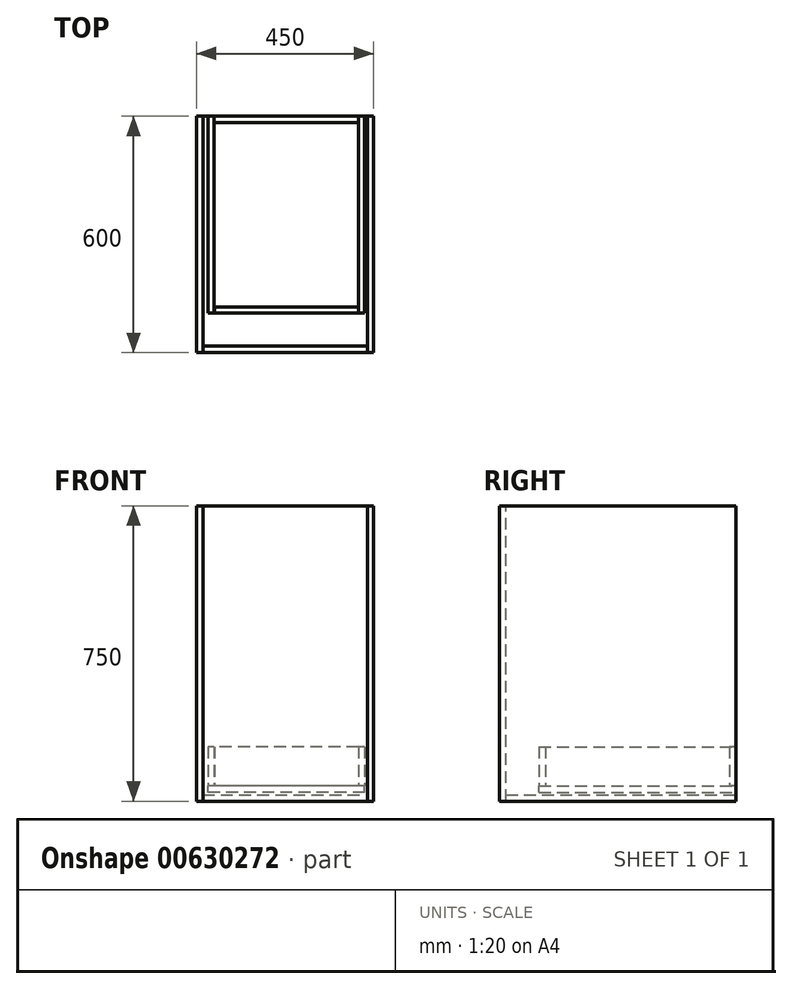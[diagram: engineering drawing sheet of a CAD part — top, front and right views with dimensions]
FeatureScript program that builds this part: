
annotation { "Feature Type Name" : "Feature", "Feature Type Description" : "" }
export const myFeature = defineFeature(function(context is Context, id is Id, definition is map)
    precondition{}
    {
        {
            var Q0;
            Q0=qCreatedBy(makeId("Top.planeOp"),FACE);
            var sketch = newSketch(context, id + "F0", { "sketchPlane" : qUnion([Q0])});
            skLineSegment(sketch, "E0.bottom", {"start": v(-209, -292) * mm, "end": v(209, -292) * mm});
            skLineSegment(sketch, "E0.top", {"start": v(-209, 292) * mm, "end": v(209, 292) * mm});
            skLineSegment(sketch, "E0.left", {"start": v(-209, -292) * mm, "end": v(-209, 292) * mm});
            skLineSegment(sketch, "E0.right", {"start": v(209, -292) * mm, "end": v(209, 292) * mm});
            skPoint(sketch, "E0.middle", {"position": v(0, 0) * mm});
            skSolve(sketch);
        }
        {
            var Q0;
            Q0 = qSketchRegion(id + "F0", true);
            extrude(context, id + "F1", {"entities" : qUnion([Q0]), "oppositeDirection" : true, "depth" : 16 * mm, "offsetDistance" : 25 * mm});
        }
        {
            var Q0;
            Q0=makeQuery(id+"F1.opExtrude","SWEPT_FACE",FACE,{"disambiguationData":[OSD([sQuery(id+"F0.wireOp",EDGE,"E0.bottom")])]});
            var sketch = newSketch(context, id + "F2", { "sketchPlane" : qUnion([Q0])});
            skLineSegment(sketch, "E1.bottom", {"start": v(-209, -16) * mm, "end": v(209, -16) * mm});
            skLineSegment(sketch, "E1.top", {"start": v(-209, 734) * mm, "end": v(209, 734) * mm});
            skLineSegment(sketch, "E1.left", {"start": v(-209, -16) * mm, "end": v(-209, 734) * mm});
            skLineSegment(sketch, "E1.right", {"start": v(209, -16) * mm, "end": v(209, 734) * mm});
            skSolve(sketch);
        }
        {
            var Q0;
            Q0 = qSketchRegion(id + "F2", true);
            extrude(context, id + "F3", {"entities" : qUnion([Q0]), "depth" : 16 * mm, "offsetDistance" : 25 * mm});
        }
        {
            var Q0;
            Q0=makeQuery(id+"F1.opExtrude","SWEPT_FACE",FACE,{"disambiguationData":[OSD([sQuery(id+"F0.wireOp",EDGE,"E0.right")])]});
            var sketch = newSketch(context, id + "F4", { "sketchPlane" : qUnion([Q0])});
            skLineSegment(sketch, "E2.bottom", {"start": v(292, -16) * mm, "end": v(-308, -16) * mm});
            skLineSegment(sketch, "E2.top", {"start": v(292, 734) * mm, "end": v(-308, 734) * mm});
            skLineSegment(sketch, "E2.left", {"start": v(292, -16) * mm, "end": v(292, 734) * mm});
            skLineSegment(sketch, "E2.right", {"start": v(-308, -16) * mm, "end": v(-308, 734) * mm});
            skSolve(sketch);
        }
        {
            var Q0;
            Q0 = qSketchRegion(id + "F4", true);
            extrude(context, id + "F5", {"entities" : qUnion([Q0]), "depth" : 16 * mm, "offsetDistance" : 25 * mm});
        }
        {
            var Q0;
            Q0=makeQuery(id+"F1.opExtrude","SWEPT_FACE",FACE,{"disambiguationData":[OSD([sQuery(id+"F0.wireOp",EDGE,"E0.left")])]});
            var sketch = newSketch(context, id + "F6", { "sketchPlane" : qUnion([Q0])});
            skLineSegment(sketch, "E3.bottom", {"start": v(-292, -16) * mm, "end": v(308, -16) * mm});
            skLineSegment(sketch, "E3.top", {"start": v(-292, 734) * mm, "end": v(308, 734) * mm});
            skLineSegment(sketch, "E3.left", {"start": v(-292, -16) * mm, "end": v(-292, 734) * mm});
            skLineSegment(sketch, "E3.right", {"start": v(308, -16) * mm, "end": v(308, 734) * mm});
            skSolve(sketch);
        }
        {
            var Q0;
            Q0 = qSketchRegion(id + "F6", true);
            extrude(context, id + "F7", {"entities" : qUnion([Q0]), "depth" : 16 * mm, "offsetDistance" : 25 * mm});
        }
        {
            var Q0;
            Q0=makeQuery(id+"F1.opExtrude","SWEPT_FACE",FACE,{"disambiguationData":[OSD([sQuery(id+"F0.wireOp",EDGE,"E0.top")])]});
            var sketch = newSketch(context, id + "F8", { "sketchPlane" : qUnion([Q0])});
            skLineSegment(sketch, "E4.bottom", {"start": v(-202.02, 6.24) * mm, "end": v(195.98, 6.24) * mm});
            skLineSegment(sketch, "E4.top", {"start": v(-202.02, 22.24) * mm, "end": v(195.98, 22.24) * mm});
            skLineSegment(sketch, "E4.left", {"start": v(-202.02, 6.24) * mm, "end": v(-202.02, 22.24) * mm});
            skLineSegment(sketch, "E4.right", {"start": v(195.98, 6.24) * mm, "end": v(195.98, 22.24) * mm});
            skSolve(sketch);
        }
        {
            var Q0;
            Q0 = qSketchRegion(id + "F8", true);
            extrude(context, id + "F9", {"entities" : qUnion([Q0]), "oppositeDirection" : true, "depth" : 500 * mm, "offsetDistance" : 25 * mm});
        }
        {
            var Q0;
            Q0=makeQuery(id+"F9.opExtrude","SWEPT_FACE",FACE,{"disambiguationData":[OSD([sQuery(id+"F8.wireOp",EDGE,"E4.top")])]});
            var sketch = newSketch(context, id + "F10", { "sketchPlane" : qUnion([Q0])});
            skLineSegment(sketch, "E5.bottom", {"start": v(202.02, -208) * mm, "end": v(186.02, -208) * mm});
            skLineSegment(sketch, "E5.top", {"start": v(202.02, 292) * mm, "end": v(186.02, 292) * mm});
            skLineSegment(sketch, "E5.left", {"start": v(202.02, -208) * mm, "end": v(202.02, 292) * mm});
            skLineSegment(sketch, "E5.right", {"start": v(186.02, -208) * mm, "end": v(186.02, 292) * mm});
            skSolve(sketch);
        }
        {
            var Q0;
            Q0 = qSketchRegion(id + "F10", true);
            extrude(context, id + "F11", {"entities" : qUnion([Q0]), "depth" : 100 * mm, "offsetDistance" : 25 * mm});
        }
        {
            var Q0;
            Q0=makeQuery(id+"F9.opExtrude","SWEPT_FACE",FACE,{"disambiguationData":[OSD([sQuery(id+"F8.wireOp",EDGE,"E4.top")])]});
            var sketch = newSketch(context, id + "F12", { "sketchPlane" : qUnion([Q0])});
            skLineSegment(sketch, "E6.bottom", {"start": v(-195.98, -208) * mm, "end": v(-179.98, -208) * mm});
            skLineSegment(sketch, "E6.top", {"start": v(-195.98, 292) * mm, "end": v(-179.98, 292) * mm});
            skLineSegment(sketch, "E6.left", {"start": v(-195.98, -208) * mm, "end": v(-195.98, 292) * mm});
            skLineSegment(sketch, "E6.right", {"start": v(-179.98, -208) * mm, "end": v(-179.98, 292) * mm});
            skSolve(sketch);
        }
        {
            var Q0;
            Q0 = qSketchRegion(id + "F12", true);
            extrude(context, id + "F13", {"entities" : qUnion([Q0]), "depth" : 100 * mm, "offsetDistance" : 25 * mm});
        }
        {
            var Q0;
            Q0=makeQuery(id+"F9.opExtrude","SWEPT_FACE",FACE,{"disambiguationData":[OSD([sQuery(id+"F8.wireOp",EDGE,"E4.top")])]});
            var sketch = newSketch(context, id + "F14", { "sketchPlane" : qUnion([Q0])});
            skLineSegment(sketch, "E7.bottom", {"start": v(-179.7, -208) * mm, "end": v(186.3, -208) * mm});
            skLineSegment(sketch, "E7.top", {"start": v(-179.7, -192) * mm, "end": v(186.3, -192) * mm});
            skLineSegment(sketch, "E7.left", {"start": v(-179.7, -208) * mm, "end": v(-179.7, -192) * mm});
            skLineSegment(sketch, "E7.right", {"start": v(186.3, -208) * mm, "end": v(186.3, -192) * mm});
            skSolve(sketch);
        }
        {
            var Q0;
            Q0 = qSketchRegion(id + "F14", true);
            extrude(context, id + "F15", {"entities" : qUnion([Q0]), "depth" : 100 * mm, "offsetDistance" : 25 * mm});
        }
        {
            var Q0;
            Q0=makeQuery(id+"F9.opExtrude","SWEPT_FACE",FACE,{"disambiguationData":[OSD([sQuery(id+"F8.wireOp",EDGE,"E4.top")])]});
            var sketch = newSketch(context, id + "F16", { "sketchPlane" : qUnion([Q0])});
            skLineSegment(sketch, "E8.bottom", {"start": v(-179.98, 292) * mm, "end": v(186.02, 292) * mm});
            skLineSegment(sketch, "E8.top", {"start": v(-179.98, 276) * mm, "end": v(186.02, 276) * mm});
            skLineSegment(sketch, "E8.left", {"start": v(-179.98, 292) * mm, "end": v(-179.98, 276) * mm});
            skLineSegment(sketch, "E8.right", {"start": v(186.02, 292) * mm, "end": v(186.02, 276) * mm});
            skSolve(sketch);
        }
        {
            var Q0;
            Q0 = qSketchRegion(id + "F16", true);
            extrude(context, id + "F17", {"entities" : qUnion([Q0]), "depth" : 100 * mm, "offsetDistance" : 25 * mm});
        }
    });
